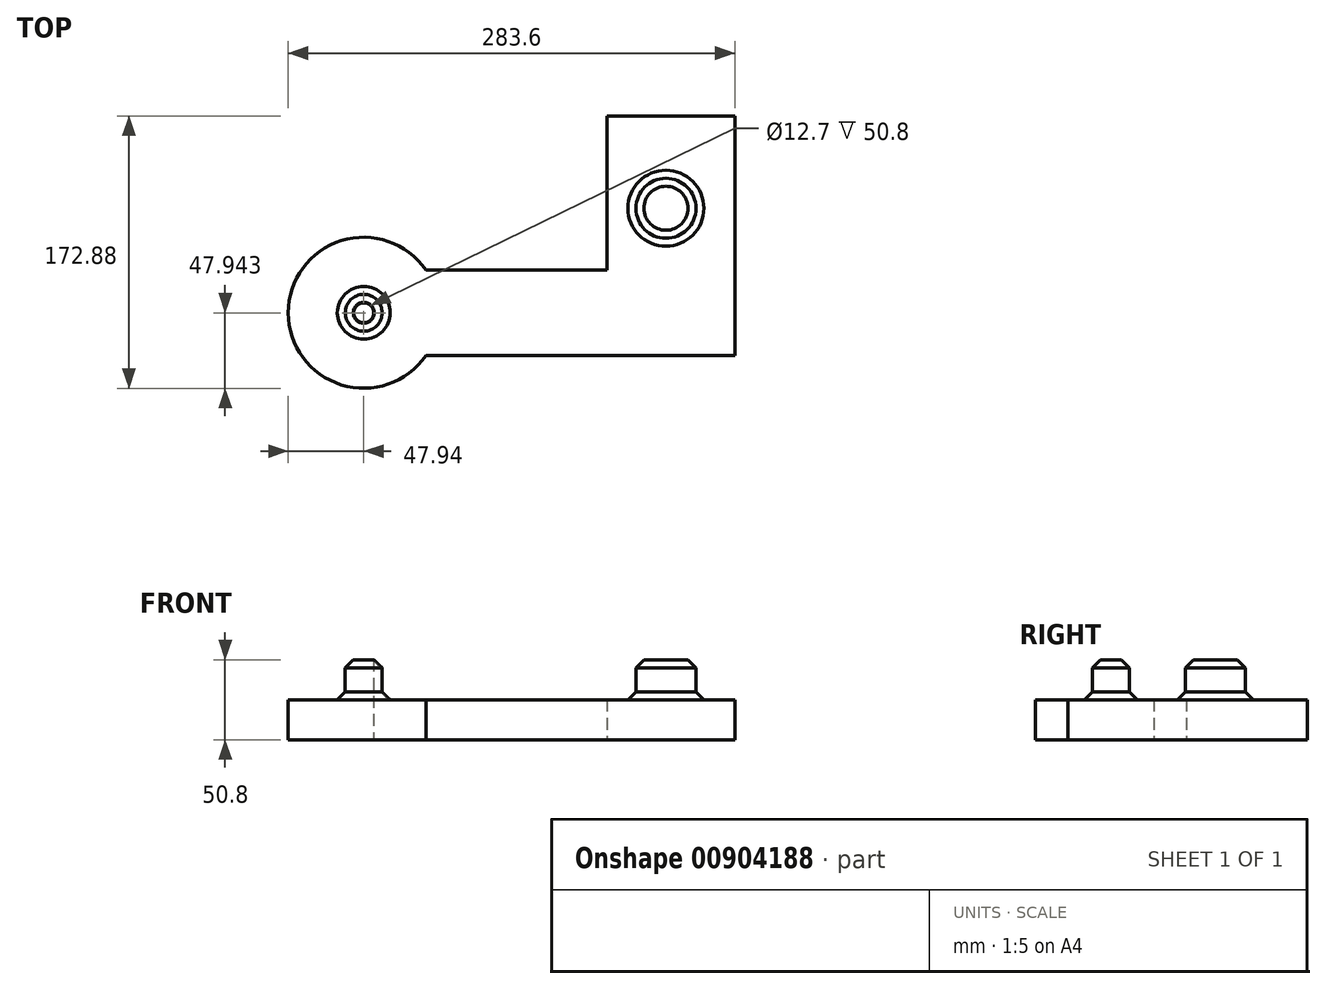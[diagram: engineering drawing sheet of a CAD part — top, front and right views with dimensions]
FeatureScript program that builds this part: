
annotation { "Feature Type Name" : "Feature", "Feature Type Description" : "" }
export const myFeature = defineFeature(function(context is Context, id is Id, definition is map)
    precondition{}
    {
        {
            var Q0;
            Q0=qCreatedBy(makeId("Top.planeOp"),FACE);
            var sketch = newSketch(context, id + "F0", { "sketchPlane" : qUnion([Q0])});
            skLineSegment(sketch, "E0.top", {"start": v(92.44, 119.09) * mm, "end": v(11.44, 119.09) * mm});
            skLineSegment(sketch, "E0.left", {"start": v(92.44, -33.13) * mm, "end": v(92.44, 119.09) * mm});
            skLineSegment(sketch, "E1.bottom", {"start": v(92.44, -33.13) * mm, "end": v(-103.8, -33.13) * mm});
            skLineSegment(sketch, "E2", {"start": v(11.44, 21.43) * mm, "end": v(-103.8, 21.43) * mm});
            skLineSegment(sketch, "E3", {"start": v(11.44, 21.43) * mm, "end": v(11.44, 119.09) * mm});
            skArc(sketch, "E4", {"start": v(-103.8, 21.43) * mm, "mid": v(-191.16, -5.85) * mm, "end": v(-103.8, -33.13) * mm});
            skCircle(sketch, "E5", {"center": v(-143.22, -5.85) * mm, "radius": 6.35 * mm});
            skCircle(sketch, "E6", {"center": v(-143.22, -5.85) * mm, "radius": 11.7 * mm});
            skCircle(sketch, "E7", {"center": v(48.7, 60.52) * mm, "radius": 19.05 * mm});
            skSolve(sketch);
        }
        {
            var Q0;
            Q0=makeQuery(id+"F0.imprint","IMPRINT",FACE,{"disambiguationData":[TD([[makeQuery(id+"F0.imprint","IMPRINT",EDGE,{"derivedFrom":sQuery(id+"F0.wireOp",EDGE,"E0.top")}),1.0]])]});
            var Q1;
            Q1=makeQuery(id+"F0.imprint","IMPRINT",FACE,{"disambiguationData":[TD([[makeQuery(id+"F0.imprint","IMPRINT",EDGE,{"derivedFrom":sQuery(id+"F0.wireOp",EDGE,"E7")}),1.0]])]});
            var Q2;
            Q2=makeQuery(id+"F0.imprint","IMPRINT",FACE,{"disambiguationData":[TD([[makeQuery(id+"F0.imprint","IMPRINT",EDGE,{"derivedFrom":sQuery(id+"F0.wireOp",EDGE,"E5")}),-1.0]])]});
            extrude(context, id + "F1", {"entities" : qUnion([Q0, Q1, Q2]), "depth" : 25.4 * mm, "offsetDistance" : 25.4 * mm});
        }
        {
            var Q0;
            Q0=makeQuery(id+"F0.imprint","IMPRINT",FACE,{"disambiguationData":[TD([[makeQuery(id+"F0.imprint","IMPRINT",EDGE,{"derivedFrom":sQuery(id+"F0.wireOp",EDGE,"E5")}),-1.0]])]});
            var Q1;
            Q1=makeQuery(id+"F0.imprint","IMPRINT",FACE,{"disambiguationData":[TD([[makeQuery(id+"F0.imprint","IMPRINT",EDGE,{"derivedFrom":sQuery(id+"F0.wireOp",EDGE,"E7")}),1.0]])]});
            extrude(context, id + "F2", {"entities" : qUnion([Q0, Q1]), "operationType" : NewBodyOperationType.ADD, "depth" : 50.8 * mm, "offsetDistance" : 25.4 * mm});
        }
        {
            var Q0;
            Q0=makeQuery(id+"F2.opExtrude","CAP_EDGE",EDGE,{"disambiguationData":[OSD([sQuery(id+"F0.wireOp",EDGE,"E7")])],"isStart":false});
            var Q1;
            Q1=makeQuery(id+"F2.boolean.opBoolean","INTERSECT",EDGE,{"derivedFrom":[makeQuery(id+"F1.opExtrude","CAP_FACE",FACE,{"disambiguationData":[OSD([sQuery(id+"F0.wireOp",EDGE,"E0.top"),sQuery(id+"F0.wireOp",EDGE,"E0.left"),sQuery(id+"F0.wireOp",EDGE,"E1.bottom"),sQuery(id+"F0.wireOp",EDGE,"E1.left"),sQuery(id+"F0.wireOp",EDGE,"E2"),sQuery(id+"F0.wireOp",EDGE,"E3"),sQuery(id+"F0.wireOp",EDGE,"E4"),sQuery(id+"F0.wireOp",EDGE,"E5")])],"isStart":false}),makeQuery(id+"F2.opExtrude","SWEPT_FACE",FACE,{"disambiguationData":[OSD([sQuery(id+"F0.wireOp",EDGE,"E6")])]})]});
            var Q2;
            Q2=makeQuery(id+"F2.opExtrude","CAP_EDGE",EDGE,{"disambiguationData":[OSD([sQuery(id+"F0.wireOp",EDGE,"E6")])],"isStart":false});
            var Q3;
            Q3=makeQuery(id+"F2.boolean.opBoolean","INTERSECT",EDGE,{"derivedFrom":[makeQuery(id+"F1.opExtrude","CAP_FACE",FACE,{"disambiguationData":[OSD([sQuery(id+"F0.wireOp",EDGE,"E0.top"),sQuery(id+"F0.wireOp",EDGE,"E0.left"),sQuery(id+"F0.wireOp",EDGE,"E1.bottom"),sQuery(id+"F0.wireOp",EDGE,"E1.left"),sQuery(id+"F0.wireOp",EDGE,"E2"),sQuery(id+"F0.wireOp",EDGE,"E3"),sQuery(id+"F0.wireOp",EDGE,"E4"),sQuery(id+"F0.wireOp",EDGE,"E5")])],"isStart":false}),makeQuery(id+"F2.opExtrude","SWEPT_FACE",FACE,{"disambiguationData":[OSD([sQuery(id+"F0.wireOp",EDGE,"E7")])]})]});
            chamfer(context, id + "F3", {"entities" : qUnion([Q0, Q1, Q2, Q3]), "width" : 5.08 * mm, "tangentPropagation" : true});
        }
    });
